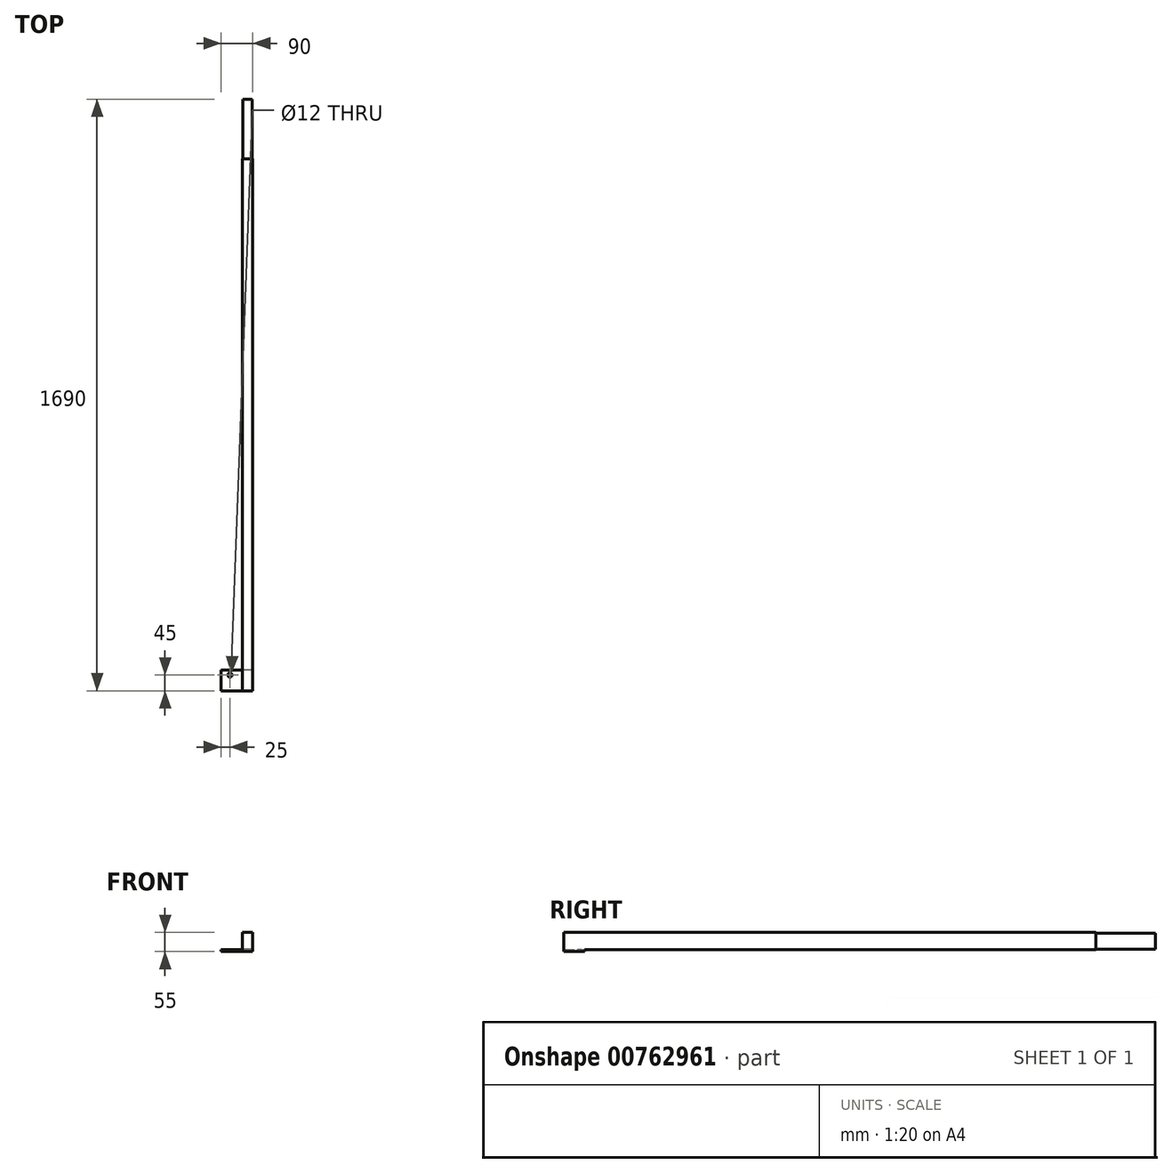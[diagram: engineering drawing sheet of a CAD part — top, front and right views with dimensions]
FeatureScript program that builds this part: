
annotation { "Feature Type Name" : "Feature", "Feature Type Description" : "" }
export const myFeature = defineFeature(function(context is Context, id is Id, definition is map)
    precondition{}
    {
        {
            var Q0;
            Q0=qCreatedBy(makeId("Front.planeOp"),FACE);
            var sketch = newSketch(context, id + "F0", { "sketchPlane" : qUnion([Q0])});
            skLineSegment(sketch, "E0.bottom", {"start": v(13, -23) * mm, "end": v(-13, -23) * mm});
            skLineSegment(sketch, "E0.top", {"start": v(13, 23) * mm, "end": v(-13, 23) * mm});
            skLineSegment(sketch, "E0.left", {"start": v(13, -23) * mm, "end": v(13, 23) * mm});
            skLineSegment(sketch, "E0.right", {"start": v(-13, -23) * mm, "end": v(-13, 23) * mm});
            skPoint(sketch, "E0.middle", {"position": v(0, 0) * mm});
            skSolve(sketch);
        }
        {
            var Q0;
            Q0=qSketchRegion(id+"F0",true);
            extrude(context, id + "F1", {"entities" : qUnion([Q0]), "depth" : 170 * mm, "offsetDistance" : 25 * mm});
        }
        {
            var Q0;
            Q0=makeQuery(id+"F1.opExtrude","CAP_FACE",FACE,{"disambiguationData":[OSD([sQuery(id+"F0.wireOp",EDGE,"E0.bottom"),sQuery(id+"F0.wireOp",EDGE,"E0.top"),sQuery(id+"F0.wireOp",EDGE,"E0.left"),sQuery(id+"F0.wireOp",EDGE,"E0.right")])],"isStart":false});
            var sketch = newSketch(context, id + "F2", { "sketchPlane" : qUnion([Q0])});
            skLineSegment(sketch, "E1.bottom", {"start": v(15, -25) * mm, "end": v(-15, -25) * mm});
            skLineSegment(sketch, "E1.top", {"start": v(15, 25) * mm, "end": v(-15, 25) * mm});
            skLineSegment(sketch, "E1.left", {"start": v(15, -25) * mm, "end": v(15, 25) * mm});
            skLineSegment(sketch, "E1.right", {"start": v(-15, -25) * mm, "end": v(-15, 25) * mm});
            skPoint(sketch, "E1.middle", {"position": v(0, 0) * mm});
            skSolve(sketch);
        }
        {
            var Q0;
            Q0=qSketchRegion(id+"F2",true);
            extrude(context, id + "F3", {"entities" : qUnion([Q0]), "operationType" : NewBodyOperationType.ADD, "depth" : 1520 * mm, "offsetDistance" : 25 * mm});
        }
        {
            var Q0;
            Q0=makeQuery(id+"F3.opExtrude","SWEPT_FACE",FACE,{"disambiguationData":[OSD([sQuery(id+"F2.wireOp",EDGE,"E1.bottom")])]});
            var sketch = newSketch(context, id + "F4", { "sketchPlane" : qUnion([Q0])});
            skLineSegment(sketch, "E2.bottom", {"start": v(-15, 1690) * mm, "end": v(15, 1690) * mm});
            skLineSegment(sketch, "E2.top", {"start": v(-15, 1630) * mm, "end": v(15, 1630) * mm});
            skLineSegment(sketch, "E2.left", {"start": v(-15, 1690) * mm, "end": v(-15, 1630) * mm});
            skLineSegment(sketch, "E2.right", {"start": v(15, 1690) * mm, "end": v(15, 1630) * mm});
            skLineSegment(sketch, "E3.bottom", {"start": v(15, 1690) * mm, "end": v(75, 1690) * mm});
            skLineSegment(sketch, "E3.top", {"start": v(15, 1630) * mm, "end": v(75, 1630) * mm});
            skLineSegment(sketch, "E3.right", {"start": v(75, 1690) * mm, "end": v(75, 1630) * mm});
            skLineSegment(sketch, "E4", {"start": v(15, 1645) * mm, "end": v(50, 1645) * mm});
            skCircle(sketch, "E5", {"center": v(50, 1645) * mm, "radius": 6 * mm});
            skLineSegment(sketch, "E6", {"start": v(-15, 1690) * mm, "end": v(15, 1690) * mm, "construction": true});
            skLineSegment(sketch, "E7", {"start": v(0, 1690) * mm, "end": v(0, 1630) * mm, "construction": true});
            skLineSegment(sketch, "E8.MirrorCS", {"start": v(-15, 1690) * mm, "end": v(-75, 1690) * mm});
            skCircle(sketch, "E9.MirrorC", {"center": v(-50, 1645) * mm, "radius": 6 * mm});
            skLineSegment(sketch, "E10.MirrorCS", {"start": v(-15, 1630) * mm, "end": v(-75, 1630) * mm});
            skLineSegment(sketch, "E11.MirrorCS", {"start": v(-75, 1690) * mm, "end": v(-75, 1630) * mm});
            skSolve(sketch);
        }
        {
            var Q0;
            Q0=makeQuery(id+"F4.imprint","IMPRINT",FACE,{"disambiguationData":[TD([[makeQuery(id+"F4.imprint","IMPRINT",EDGE,{"derivedFrom":sQuery(id+"F4.wireOp",EDGE,"E2.left")}),-1.0]])]});
            var Q1;
            {var subQ2=sQuery(id+"F4.wireOp",EDGE,"E2.bottom");Q1=makeQuery(id+"F4.imprint","IMPRINT",FACE,{"disambiguationData":[TD([[makeQuery(id+"F4.imprint","IMPRINT",EDGE,{"derivedFrom":subQ2}),1.0]])]});}
            extrude(context, id + "F5", {"entities" : qUnion([Q0, Q1]), "operationType" : NewBodyOperationType.ADD, "depth" : 5 * mm, "offsetDistance" : 25 * mm});
        }
    });
